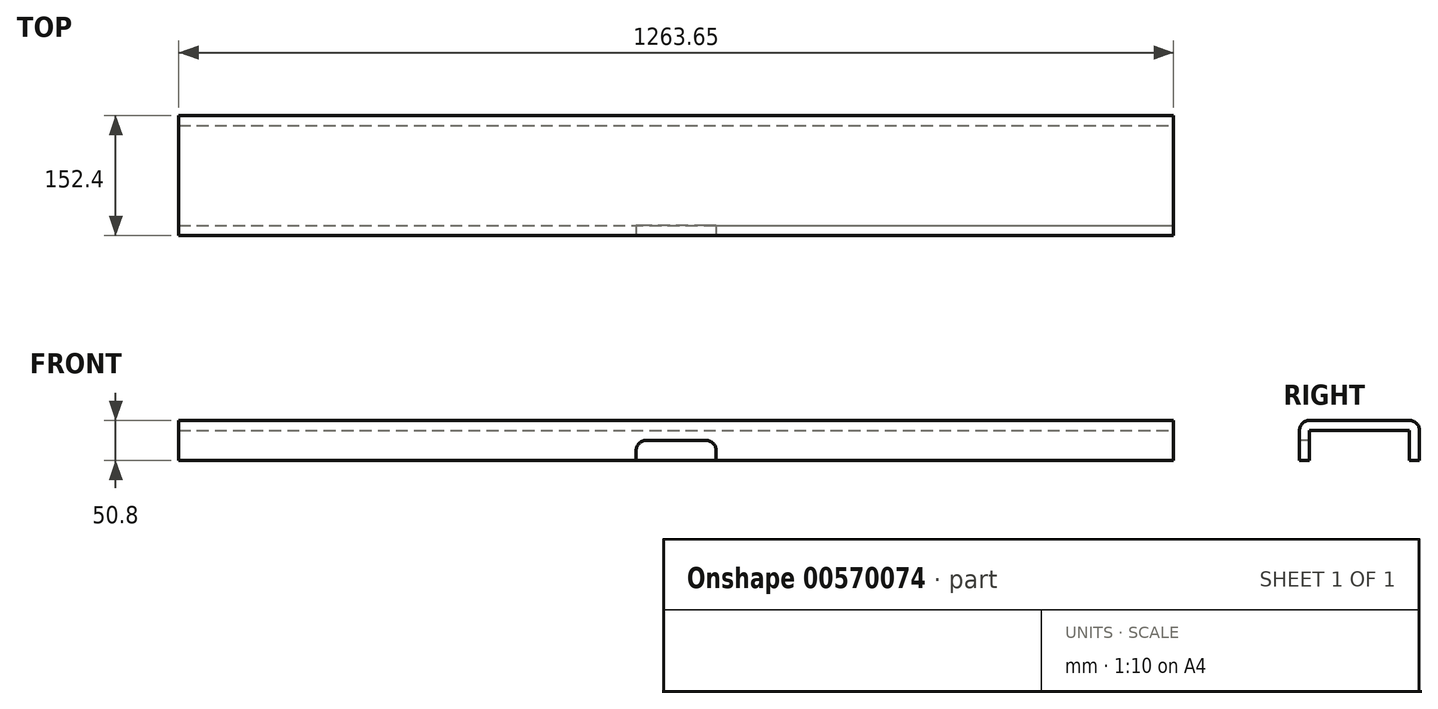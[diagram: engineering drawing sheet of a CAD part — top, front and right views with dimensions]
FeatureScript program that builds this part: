
annotation { "Feature Type Name" : "Feature", "Feature Type Description" : "" }
export const myFeature = defineFeature(function(context is Context, id is Id, definition is map)
    precondition{}
    {
        {
            var Q0;
            Q0=qCreatedBy(makeId("Right.planeOp"),FACE);
            var sketch = newSketch(context, id + "F0", { "sketchPlane" : qUnion([Q0])});
            skLineSegment(sketch, "E0", {"start": v(0, 0) * mm, "end": v(-12.7, 0) * mm});
            skLineSegment(sketch, "E1", {"start": v(-12.7, 0) * mm, "end": v(-12.7, 38.1) * mm});
            skLineSegment(sketch, "E2", {"start": v(0, 50.8) * mm, "end": v(127, 50.8) * mm});
            skLineSegment(sketch, "E3", {"start": v(139.7, 38.1) * mm, "end": v(139.7, 0) * mm});
            skLineSegment(sketch, "E4", {"start": v(139.7, 0) * mm, "end": v(127, 0) * mm});
            skLineSegment(sketch, "E5", {"start": v(127, 0) * mm, "end": v(127, 38.1) * mm});
            skLineSegment(sketch, "E6", {"start": v(127, 38.1) * mm, "end": v(0, 38.1) * mm});
            skLineSegment(sketch, "E7", {"start": v(0, 38.1) * mm, "end": v(0, 0) * mm});
            skPoint(sketch, "E8.visualSharp", {"position": v(-12.7, 50.8) * mm});
            skArc(sketch, "E8.filletArc", {"start": v(0, 50.8) * mm, "mid": v(-8.98, 47.08) * mm, "end": v(-12.7, 38.1) * mm});
            skPoint(sketch, "E9.visualSharp", {"position": v(139.7, 50.8) * mm});
            skArc(sketch, "E9.filletArc", {"start": v(139.7, 38.1) * mm, "mid": v(135.98, 47.08) * mm, "end": v(127, 50.8) * mm});
            skSolve(sketch);
        }
        {
            var Q0;
            Q0 = qSketchRegion(id + "F0", true);
            extrude(context, id + "F1", {"entities" : qUnion([Q0]), "oppositeDirection" : true, "depth" : 1263.65 * mm, "offsetDistance" : 25.4 * mm});
        }
        {
            var Q0;
            Q0=makeQuery(id+"F1.opExtrude","SWEPT_FACE",FACE,{"disambiguationData":[OSD([sQuery(id+"F0.wireOp",EDGE,"E1")])]});
            var sketch = newSketch(context, id + "F2", { "sketchPlane" : qUnion([Q0])});
            skLineSegment(sketch, "E10", {"start": v(0, 0) * mm, "end": v(-581.02, 0) * mm});
            skLineSegment(sketch, "E11", {"start": v(-581.02, 0) * mm, "end": v(-581.02, 12.7) * mm});
            skLineSegment(sketch, "E12", {"start": v(-593.73, 25.4) * mm, "end": v(-669.92, 25.4) * mm});
            skLineSegment(sketch, "E13", {"start": v(-682.62, 12.7) * mm, "end": v(-682.62, 0) * mm});
            skPoint(sketch, "E14.visualSharp", {"position": v(-682.62, 25.4) * mm});
            skArc(sketch, "E14.filletArc", {"start": v(-669.92, 25.4) * mm, "mid": v(-678.9, 21.68) * mm, "end": v(-682.63, 12.7) * mm});
            skPoint(sketch, "E15.visualSharp", {"position": v(-581.02, 25.4) * mm});
            skArc(sketch, "E15.filletArc", {"start": v(-581.02, 12.7) * mm, "mid": v(-584.74, 21.68) * mm, "end": v(-593.73, 25.4) * mm});
            skSolve(sketch);
        }
        {
            var Q0;
            Q0 = qSketchRegion(id + "F2", true);
            var Q1;
            {var subQ0=sQuery(id+"F2.wireOp",EDGE,"E11");Q1=makeQuery(id+"F2.imprint","IMPRINT",FACE,{"disambiguationData":[TD([[makeQuery(id+"F2.imprint","IMPRINT",EDGE,{"derivedFrom":subQ0}),1.0]])]});}
            extrude(context, id + "F3", {"entities" : qUnion([Q0, Q1]), "operationType" : NewBodyOperationType.REMOVE, "oppositeDirection" : true, "depth" : 12.7 * mm, "offsetDistance" : 25.4 * mm});
        }
    });
